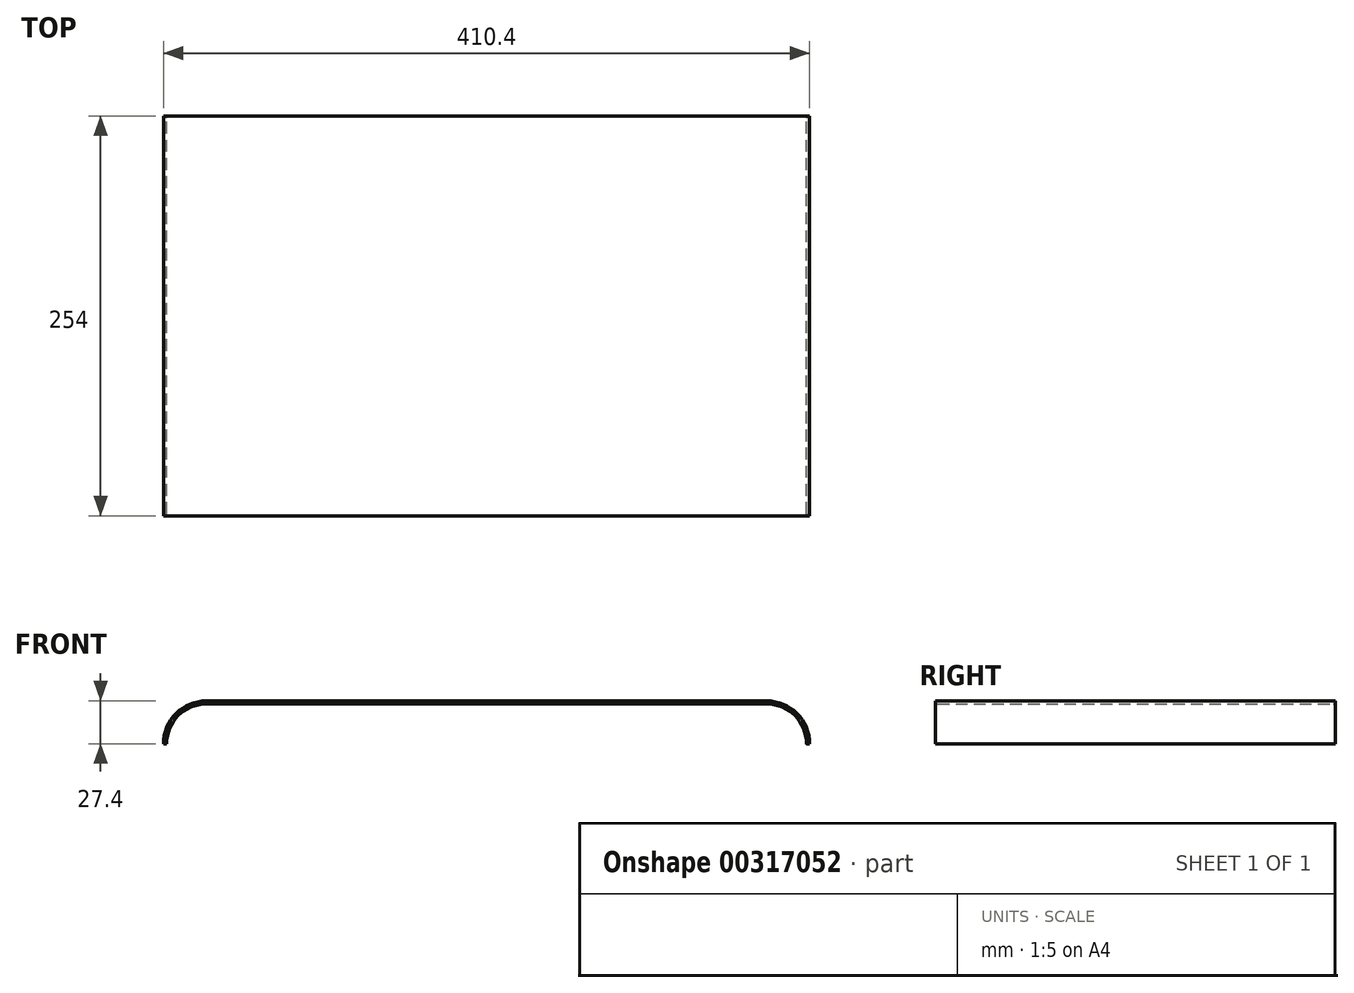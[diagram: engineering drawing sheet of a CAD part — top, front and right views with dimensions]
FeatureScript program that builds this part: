
annotation { "Feature Type Name" : "Feature", "Feature Type Description" : "" }
export const myFeature = defineFeature(function(context is Context, id is Id, definition is map)
    precondition{}
    {
        {
            var Q0;
            Q0=qCreatedBy(makeId("Front.planeOp"),FACE);
            var sketch = newSketch(context, id + "F0", { "sketchPlane" : qUnion([Q0])});
            skLineSegment(sketch, "E0", {"start": v(0, 0) * mm, "end": v(355.6, 0) * mm});
            skLineSegment(sketch, "E1", {"start": v(0, 101.1) * mm, "end": v(0, -98.66) * mm, "construction": true});
            skPoint(sketch, "E2", {"position": v(0, -25.4) * mm});
            skArc(sketch, "E3", {"start": v(0, 0) * mm, "mid": v(-17.96, -7.44) * mm, "end": v(-25.4, -25.4) * mm});
            skPoint(sketch, "E4", {"position": v(-25.4, -25.4) * mm});
            skLineSegment(sketch, "E5", {"start": v(177.8, 79.9) * mm, "end": v(177.8, -94.58) * mm, "construction": true});
            skPoint(sketch, "E5.startSnap0", {"position": v(177.8, 0) * mm});
            skArc(sketch, "E6.MirrorCS", {"start": v(355.6, 0) * mm, "mid": v(373.56, -7.44) * mm, "end": v(381, -25.4) * mm});
            skArc(sketch, "E7.0", {"start": v(0, 2) * mm, "mid": v(-19.37, -6.03) * mm, "end": v(-27.4, -25.4) * mm});
            skLineSegment(sketch, "E7.1", {"start": v(0, 2) * mm, "end": v(355.6, 2) * mm});
            skArc(sketch, "E7.2", {"start": v(355.6, 2) * mm, "mid": v(374.97, -6.03) * mm, "end": v(383, -25.4) * mm});
            skLineSegment(sketch, "E8", {"start": v(-25.4, -25.4) * mm, "end": v(-27.4, -25.4) * mm});
            skLineSegment(sketch, "E9", {"start": v(383, -25.4) * mm, "end": v(381, -25.4) * mm});
            skSolve(sketch);
        }
        {
            var Q0;
            Q0=qSketchRegion(id+"F0",true);
            extrude(context, id + "F1", {"entities" : qUnion([Q0]), "depth" : 254 * mm});
        }
        {
            var Q0;
            Q0=makeQuery(id+"F1.opExtrude","CAP_EDGE",EDGE,{"disambiguationData":[OSD([sQuery(id+"F0.wireOp",EDGE,"E0")])],"isStart":false});
            var Q1;
            Q1=makeQuery(id+"F1.opExtrude","CAP_EDGE",EDGE,{"disambiguationData":[OSD([sQuery(id+"F0.wireOp",EDGE,"E0")])],"isStart":true});
            fillet(context, id + "F2", {"entities" : qUnion([Q0, Q1]), "radius" : 1.27 * mm, "tangentPropagation" : true, "allowEdgeOverflow" : false});
        }
    });
